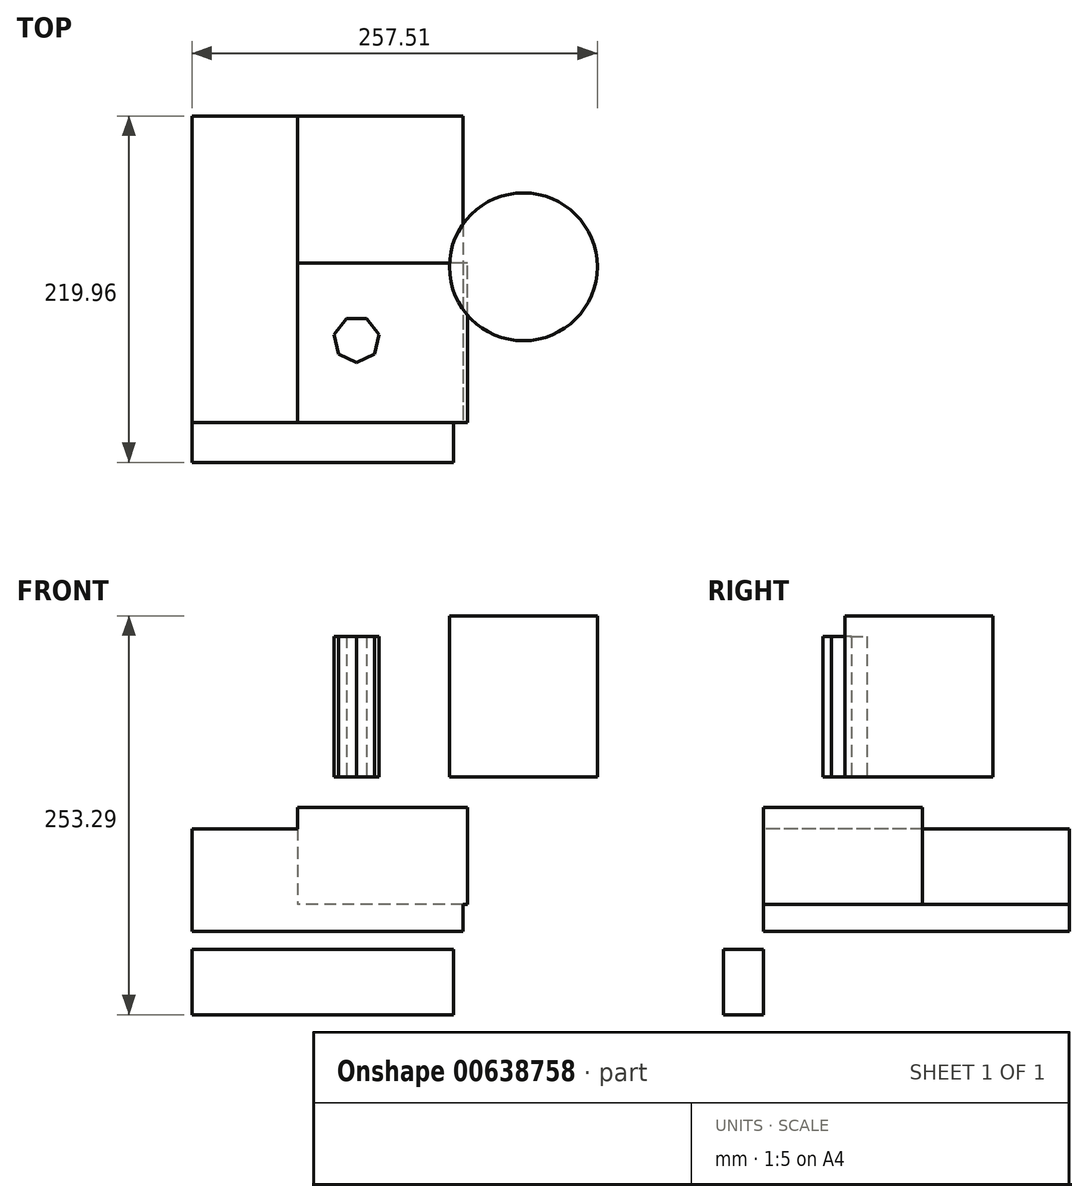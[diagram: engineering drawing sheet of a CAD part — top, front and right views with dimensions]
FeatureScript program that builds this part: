
annotation { "Feature Type Name" : "Feature", "Feature Type Description" : "" }
export const myFeature = defineFeature(function(context is Context, id is Id, definition is map)
    precondition{}
    {
        {
            var Q0;
            Q0=qCreatedBy(makeId("Top.planeOp"),FACE);
            var sketch = newSketch(context, id + "F0", { "sketchPlane" : qUnion([Q0])});
            skCircle(sketch, "E0", {"center": v(-7.18, -2.24) * mm, "radius": 46.96 * mm});
            skPoint(sketch, "E0.first.point", {"position": v(-42.33, 28.89) * mm});
            skPoint(sketch, "E0.second.point", {"position": v(28.43, -32.87) * mm});
            skPoint(sketch, "E0.third.point", {"position": v(16.29, 38.43) * mm});
            skSolve(sketch);
        }
        {
            var Q0;
            Q0=makeQuery(id+"F0.imprint","IMPRINT",FACE,{"disambiguationData":[TD([[makeQuery(id+"F0.imprint","IMPRINT",EDGE,{"derivedFrom":sQuery(id+"F0.wireOp",EDGE,"E0")}),1.0]])]});
            extrude(context, id + "F1", {"entities" : qUnion([Q0]), "depth" : 102.36 * mm, "offsetDistance" : 25.4 * mm});
        }
        {
            var Q0;
            Q0=qCreatedBy(makeId("Front.planeOp"),FACE);
            var sketch = newSketch(context, id + "F2", { "sketchPlane" : qUnion([Q0])});
            skLineSegment(sketch, "E1.bottom", {"start": v(-42.53, -19.37) * mm, "end": v(-150.54, -19.37) * mm});
            skLineSegment(sketch, "E1.top", {"start": v(-42.53, -80.92) * mm, "end": v(-150.54, -80.92) * mm});
            skLineSegment(sketch, "E1.left", {"start": v(-42.53, -19.37) * mm, "end": v(-42.53, -80.92) * mm});
            skLineSegment(sketch, "E1.right", {"start": v(-150.54, -19.37) * mm, "end": v(-150.54, -80.92) * mm});
            skSolve(sketch);
        }
        {
            var Q0;
            Q0=makeQuery(id+"F2.imprint","IMPRINT",FACE,{"disambiguationData":[TD([[makeQuery(id+"F2.imprint","IMPRINT",EDGE,{"derivedFrom":sQuery(id+"F2.wireOp",EDGE,"E1.bottom")}),1.0]])]});
            extrude(context, id + "F3", {"entities" : qUnion([Q0]), "depth" : 101.1 * mm, "offsetDistance" : 25.4 * mm});
        }
        {
            var Q0;
            Q0=qCreatedBy(makeId("Top.planeOp"),FACE);
            var sketch = newSketch(context, id + "F4", { "sketchPlane" : qUnion([Q0])});
            skCircle(sketch, "E2.cCircle", {"center": v(-113.12, -48.44) * mm, "radius": 13.32 * mm, "construction": true});
            skLineSegment(sketch, "E2.0", {"start": v(-119.54, -35.11) * mm, "end": v(-106.7, -35.11) * mm});
            skLineSegment(sketch, "E2.1", {"start": v(-106.7, -35.11) * mm, "end": v(-98.7, -45.15) * mm});
            skLineSegment(sketch, "E2.2", {"start": v(-98.7, -45.15) * mm, "end": v(-101.56, -57.65) * mm});
            skLineSegment(sketch, "E2.3", {"start": v(-101.56, -57.65) * mm, "end": v(-113.12, -63.22) * mm});
            skLineSegment(sketch, "E2.4", {"start": v(-113.12, -63.22) * mm, "end": v(-124.68, -57.65) * mm});
            skLineSegment(sketch, "E2.5", {"start": v(-124.68, -57.65) * mm, "end": v(-127.54, -45.15) * mm});
            skLineSegment(sketch, "E2.6", {"start": v(-127.54, -45.15) * mm, "end": v(-119.54, -35.11) * mm});
            skPoint(sketch, "E2.0.midPoint", {"position": v(-113.12, -35.11) * mm});
            skSolve(sketch);
        }
        {
            var Q0;
            Q0=makeQuery(id+"F4.imprint","IMPRINT",FACE,{"disambiguationData":[TD([[makeQuery(id+"F4.imprint","IMPRINT",EDGE,{"derivedFrom":sQuery(id+"F4.wireOp",EDGE,"E2.0")}),-1.0]])]});
            extrude(context, id + "F5", {"entities" : qUnion([Q0]), "depth" : 89.4 * mm, "offsetDistance" : 25.4 * mm});
        }
        {
            var Q0;
            Q0=makeQuery(id+"F3.opExtrude","SWEPT_FACE",FACE,{"disambiguationData":[OSD([sQuery(id+"F2.wireOp",EDGE,"E1.bottom")])]});
            var sketch = newSketch(context, id + "F6", { "sketchPlane" : qUnion([Q0])});
            skSolve(sketch);
        }
        {
            var Q0;
            {var subQ0=sQuery(id+"F2.wireOp",EDGE,"E1.bottom");Q0=makeQuery(id+"F6.imprint","IMPRINT",FACE,{"disambiguationData":[TD([[makeQuery(id+"F6.imprint","IMPRINT",EDGE,{"derivedFrom":makeQuery(id+"F3.opExtrude","CAP_EDGE",EDGE,{"disambiguationData":[OSD([subQ0])],"isStart":true})}),1.0]])]});}
            var sketch = newSketch(context, id + "F7", { "sketchPlane" : qUnion([Q0])});
            skFitSpline(sketch, "E3", {"points": [v(-212.6, 119.18) * mm, v(-112.47, 187.79) * mm, v(-112.47, 187.79) * mm], "startDerivative": vector(150.24, 102.92) * mm, "endDerivative": vector(-0.02, 0.04) * mm});
            skFitSpline(sketch, "E4", {"points": [v(-197.56, 113.01) * mm, v(-112.47, 173.88) * mm, v(0, 0) * mm, v(-112.47, -209.14) * mm], "startDerivative": vector(304.84, 396.36) * mm, "endDerivative": vector(-458.82, -501.15) * mm});
            skSolve(sketch);
        }
        {
            var Q0;
            Q0=sQuery(id+"F7.wireOp",EDGE,"E4");
            extrude(context, id + "F8", {"bodyType" : ToolBodyType.SURFACE, "surfaceEntities" : qUnion([Q0]), "depth" : 25.4 * mm, "offsetDistance" : 25.4 * mm});
        }
        {
            var Q0;
            Q0=makeQuery(id+"F3.opExtrude","CAP_FACE",FACE,{"disambiguationData":[OSD([sQuery(id+"F2.wireOp",EDGE,"E1.bottom"),sQuery(id+"F2.wireOp",EDGE,"E1.top"),sQuery(id+"F2.wireOp",EDGE,"E1.left"),sQuery(id+"F2.wireOp",EDGE,"E1.right")])],"isStart":false});
            var sketch = newSketch(context, id + "F9", { "sketchPlane" : qUnion([Q0])});
            skLineSegment(sketch, "E5.bottom", {"start": v(-217.73, -32.9) * mm, "end": v(-45.6, -32.9) * mm});
            skLineSegment(sketch, "E5.top", {"start": v(-217.73, -97.96) * mm, "end": v(-45.6, -97.96) * mm});
            skLineSegment(sketch, "E5.left", {"start": v(-217.73, -32.9) * mm, "end": v(-217.73, -97.96) * mm});
            skLineSegment(sketch, "E5.right", {"start": v(-45.6, -32.9) * mm, "end": v(-45.6, -97.96) * mm});
            skSolve(sketch);
        }
        {
            var Q0;
            {var subQ1=sQuery(id+"F9.wireOp",EDGE,"E5.top");Q0=makeQuery(id+"F9.imprint","IMPRINT",FACE,{"disambiguationData":[TD([[makeQuery(id+"F9.imprint","IMPRINT",EDGE,{"derivedFrom":subQ1}),1.0]])]});}
            extrude(context, id + "F10", {"entities" : qUnion([Q0]), "operationType" : NewBodyOperationType.ADD, "oppositeDirection" : true, "depth" : 194.56 * mm, "offsetDistance" : 25.4 * mm});
        }
        {
            var Q0;
            {var subQ0=sQuery(id+"F2.wireOp",EDGE,"E1.right");var subQ1=sQuery(id+"F2.wireOp",EDGE,"E1.top");Q0=makeQuery(id+"F10.boolean.opBoolean","MERGE",FACE,{"derivedFrom":[makeQuery(id+"F3.opExtrude","CAP_FACE",FACE,{"disambiguationData":[OSD([sQuery(id+"F2.wireOp",EDGE,"E1.bottom"),subQ1,sQuery(id+"F2.wireOp",EDGE,"E1.left"),subQ0])],"isStart":false}),makeQuery(id+"F10.opExtrude","CAP_FACE",FACE,{"disambiguationData":[OSD([subQ1,subQ0,sQuery(id+"F9.wireOp",EDGE,"E5.bottom"),sQuery(id+"F9.wireOp",EDGE,"E5.top"),sQuery(id+"F9.wireOp",EDGE,"E5.left"),sQuery(id+"F9.wireOp",EDGE,"E5.right")])],"isStart":true})]});}
            var sketch = newSketch(context, id + "F11", { "sketchPlane" : qUnion([Q0])});
            skLineSegment(sketch, "E6.bottom", {"start": v(-219.08, -109.57) * mm, "end": v(-51.67, -109.57) * mm});
            skLineSegment(sketch, "E6.top", {"start": v(-219.08, -97.96) * mm, "end": v(-51.67, -97.96) * mm});
            skLineSegment(sketch, "E6.left", {"start": v(-219.08, -109.57) * mm, "end": v(-219.08, -97.96) * mm});
            skLineSegment(sketch, "E6.right", {"start": v(-51.67, -109.57) * mm, "end": v(-51.67, -97.96) * mm});
            skLineSegment(sketch, "E7.bottom", {"start": v(-51.67, -99.04) * mm, "end": v(-217.73, -99.04) * mm});
            skLineSegment(sketch, "E7.top", {"start": v(-51.67, -150.93) * mm, "end": v(-217.73, -150.93) * mm});
            skLineSegment(sketch, "E7.left", {"start": v(-51.67, -99.04) * mm, "end": v(-51.67, -150.93) * mm});
            skLineSegment(sketch, "E7.right", {"start": v(-217.73, -99.04) * mm, "end": v(-217.73, -150.93) * mm});
            skSolve(sketch);
        }
        {
            var Q0;
            {var subQ5=sQuery(id+"F11.wireOp",EDGE,"E7.top");Q0=makeQuery(id+"F11.imprint","IMPRINT",FACE,{"disambiguationData":[TD([[makeQuery(id+"F11.imprint","IMPRINT",EDGE,{"derivedFrom":subQ5}),-1.0]])]});}
            extrude(context, id + "F12", {"entities" : qUnion([Q0]), "depth" : 25.4 * mm, "offsetDistance" : 25.4 * mm});
        }
        {
            var Q0;
            {var subQ0=sQuery(id+"F2.wireOp",EDGE,"E1.right");var subQ1=sQuery(id+"F2.wireOp",EDGE,"E1.top");Q0=makeQuery(id+"F10.boolean.opBoolean","MERGE",FACE,{"derivedFrom":[makeQuery(id+"F3.opExtrude","CAP_FACE",FACE,{"disambiguationData":[OSD([sQuery(id+"F2.wireOp",EDGE,"E1.bottom"),subQ1,sQuery(id+"F2.wireOp",EDGE,"E1.left"),subQ0])],"isStart":false}),makeQuery(id+"F10.opExtrude","CAP_FACE",FACE,{"disambiguationData":[OSD([subQ1,subQ0,sQuery(id+"F9.wireOp",EDGE,"E5.bottom"),sQuery(id+"F9.wireOp",EDGE,"E5.top"),sQuery(id+"F9.wireOp",EDGE,"E5.left"),sQuery(id+"F9.wireOp",EDGE,"E5.right")])],"isStart":true})]});}
            var sketch = newSketch(context, id + "F13", { "sketchPlane" : qUnion([Q0])});
            skFitSpline(sketch, "E8", {"points": [v(-172.5, -86) * mm, v(-216.38, -152) * mm, v(-215.7, -151.8) * mm], "startDerivative": vector(-73.53, -106.24) * mm, "endDerivative": vector(10.25, 5.47) * mm});
            skSolve(sketch);
        }
        {
            var Q0;
            Q0=sQuery(id+"F13.wireOp",EDGE,"E8");
            extrude(context, id + "F14", {"bodyType" : ToolBodyType.SURFACE, "surfaceEntities" : qUnion([Q0]), "oppositeDirection" : true, "depth" : 11.94 * mm, "offsetDistance" : 25.4 * mm});
        }
    });
